# Revit family: HERZ-AS-T-90-Heizkörperregulierventil DG 6823
name_source: partatom
category: Rohrzubehör
revit_build: Autodesk Revit 2018 (Build: 20190510_1515(x64)
units: mm (PartAtom-declared; Revit-internal decimal feet)

## family parameters
Arbeitsebenenbasiert = Nein
Beim Laden mit Abzugskörper schneiden = Nein
Bemaßung runder Anschluss = Durchmesser verwenden
Gemeinsam genutzt = Nein
Immer vertikal = Ja
OmniClass-Nummer = 23.65.55.14
OmniClass-Titel = Valves for Liquid Services
Teiletyp = Unterbricht

## types (1)
- HERZ-AS-T-90-Heizkörperregulierventil DG 6823
    Anwendungsgebiet = Warmwasserheizungsanlagen, wo auf genauestes Einregulieren und sparsamsten Betrieb Wert gelegt wird. Einbau in Klimaanlagen, zur genauen Einregulierung von Kühl- und Heizregistern, auch als Strangregulierventil geeignet.
    Ausführungen = Alle Modelle werden in vernickelter Ausführung mit weißem Schraubplättchen, Handrad und Handradschutzkappe geliefert.
    Gehäuse = vernickeltes Messing
    H01 = 17 mm
    H02 = 24.5 mm  [stored 0.0803806 ft]
    Handrad = Kunststoff, weiß
    Hersteller = HERZ Armaturen Ges.m.b.H.
    LO1 = 10.5 mm  [stored 0.0344488 ft]
    Max.Betriebsdruck = 1000000.0 Pa
    Max.Betriebstemperatur = 120 °C
    Medium = Heizwasserqualität entsprechend ÖNORM H 5195 bzw. VDI-Richtllinie 2035.
    R01 = 10.5 mm  [stored 0.0344488 ft]
    R02 = 11.5 mm  [stored 0.0377297 ft]
    R03 = 28 mm  [stored 0.0918635 ft]
    R04 = 2 mm  [stored 0.00656168 ft]
    R05 = 25 mm  [stored 0.082021 ft]
    S01 = 10 mm  [stored 0.0328084 ft]
    S04 = 45 mm  [stored 0.147638 ft]
    SCRNCODE = 05;00;02
    SCRNSEQ = ARM;ARM_TYP="ALLF";2
    URL = www.herz-armaturen.at

note: [stored X ft] marks values corroborated as IEEE doubles in the binary element streams (Revit-internal decimal feet)
